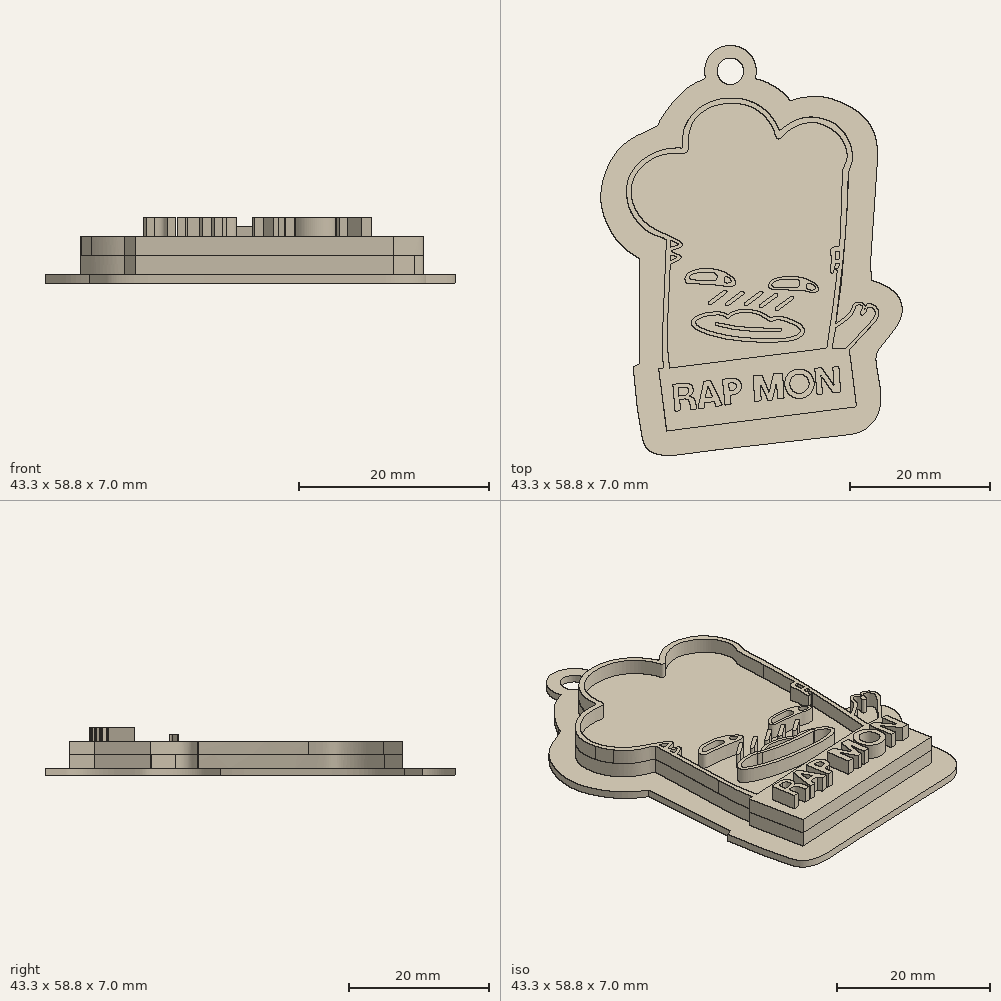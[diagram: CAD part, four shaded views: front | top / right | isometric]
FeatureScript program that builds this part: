
annotation { "Feature Type Name" : "Feature", "Feature Type Description" : "" }
export const myFeature = defineFeature(function(context is Context, id is Id, definition is map)
    precondition{}
    {
        {
            var Q0;
            Q0=qCreatedBy(makeId("Top.planeOp"),FACE);
            var sketch = newSketch(context, id + "F0", { "sketchPlane" : qUnion([Q0])});
            skFitSpline(sketch, "E0", {"points": [v(11.6, -10.29) * mm, v(12.19, -6.25) * mm, v(12.52, -3) * mm, v(12.76, 0) * mm, v(13.08, 4.27) * mm, v(13.3, 8.16) * mm, v(13.44, 11.1) * mm, v(13.87, 12.48) * mm, v(13.83, 14.28) * mm, v(13.03, 16.3) * mm, v(11.52, 17.89) * mm, v(9.06, 18.87) * mm, v(6.77, 18.83) * mm, v(4.71, 17.89) * mm, v(3.64, 17.07) * mm], "startDerivative": vector(7.03, 48) * mm, "endDerivative": vector(-18.68, -15.7) * mm});
            skFitSpline(sketch, "E1", {"points": [v(3.64, 17.07) * mm, v(3.54, 16.95) * mm], "startDerivative": vector(-0.1, -0.12) * mm, "endDerivative": vector(-0.1, -0.12) * mm});
            skFitSpline(sketch, "E2", {"points": [v(3.54, 16.95) * mm, v(3.13, 17.78) * mm, v(2.16, 19.22) * mm, v(0.67, 20.53) * mm, v(-0.94, 21.32) * mm, v(-2.8, 21.68) * mm, v(-4.71, 21.6) * mm, v(-6.36, 21.15) * mm, v(-7.6, 20.54) * mm, v(-8.9, 19.4) * mm, v(-9.89, 18.02) * mm, v(-10.33, 16.75) * mm, v(-10.44, 15.26) * mm, v(-10.47, 14.71) * mm], "startDerivative": vector(-5.85, 12.75) * mm, "endDerivative": vector(-0.6, -9.84) * mm});
            skFitSpline(sketch, "E3", {"points": [v(-10.47, 14.71) * mm, v(-10.48, 14.52) * mm], "startDerivative": vector(-0.01, -0.2) * mm, "endDerivative": vector(-0.01, -0.2) * mm});
            skFitSpline(sketch, "E4", {"points": [v(-10.48, 14.52) * mm, v(-11.68, 14.52) * mm, v(-13.25, 14.28) * mm, v(-14.57, 13.77) * mm, v(-15.75, 13.07) * mm, v(-16.9, 12.1) * mm, v(-17.9, 10.7) * mm, v(-18.43, 9.11) * mm, v(-18.41, 7.32) * mm, v(-18.05, 5.82) * mm, v(-17.34, 4.5) * mm, v(-16.2, 3.19) * mm, v(-14.73, 2.19) * mm, v(-13.46, 1.71) * mm, v(-12.75, 1.35) * mm], "startDerivative": vector(-17.9, 0.57) * mm, "endDerivative": vector(12.96, -6.95) * mm});
            skFitSpline(sketch, "E5", {"points": [v(-12.75, 1.35) * mm, v(-12.75, -0.15) * mm, v(-12.85, -2.56) * mm, v(-13.05, -5.98) * mm, v(-13.18, -9.16) * mm, v(-13.35, -13.7) * mm, v(-13.2, -17.06) * mm], "startDerivative": vector(0.18, -12.05) * mm, "endDerivative": vector(1.35, -17.94) * mm});
            skFitSpline(sketch, "E6", {"points": [v(11.6, -10.29) * mm, v(11.54, -10.75) * mm], "startDerivative": vector(-0.07, -0.47) * mm, "endDerivative": vector(-0.07, -0.47) * mm});
            skFitSpline(sketch, "E7", {"points": [v(11.54, -10.75) * mm, v(12.07, -10.4) * mm, v(12.74, -9.9) * mm, v(13.3, -9.42) * mm, v(13.62, -9.01) * mm, v(13.88, -8.46) * mm, v(14.13, -7.93) * mm, v(14.54, -7.65) * mm, v(15.04, -7.6) * mm, v(15.42, -7.74) * mm, v(15.68, -8) * mm, v(15.76, -8.28) * mm, v(15.68, -8.65) * mm, v(15.45, -9.05) * mm], "startDerivative": vector(6.21, 4.08) * mm, "endDerivative": vector(-2.77, -5.72) * mm});
            skFitSpline(sketch, "E8", {"points": [v(15.45, -9.05) * mm, v(15.72, -8.65) * mm, v(15.86, -8.22) * mm, v(16.04, -7.94) * mm, v(16.33, -7.82) * mm, v(16.83, -7.91) * mm, v(17.31, -8.27) * mm, v(17.64, -8.8) * mm, v(17.72, -9.2) * mm, v(17.63, -9.78) * mm, v(17.29, -10.38) * mm, v(16.76, -10.98) * mm], "startDerivative": vector(3.5, 4.32) * mm, "endDerivative": vector(-4.78, -5.57) * mm});
            skFitSpline(sketch, "E9", {"points": [v(16.76, -10.98) * mm, v(16.27, -11.5) * mm, v(15.56, -12.24) * mm, v(14.69, -13.16) * mm, v(14.2, -13.7) * mm, v(13.62, -14.35) * mm], "startDerivative": vector(-2.64, -2.86) * mm, "endDerivative": vector(-3.05, -3.54) * mm});
            skFitSpline(sketch, "E10", {"points": [v(13.62, -14.35) * mm, v(13.5, -14.48) * mm], "startDerivative": vector(-0.12, -0.13) * mm, "endDerivative": vector(-0.12, -0.13) * mm});
            skLineSegment(sketch, "E11", {"start": v(13.5, -14.48) * mm, "end": v(14.54, -22.61) * mm});
            skLineSegment(sketch, "E12", {"start": v(14.54, -22.61) * mm, "end": v(-12.73, -26.1) * mm});
            skLineSegment(sketch, "E13", {"start": v(-12.73, -26.1) * mm, "end": v(-13.86, -17.17) * mm});
            skLineSegment(sketch, "E14", {"start": v(-13.86, -17.17) * mm, "end": v(-13.32, -17.1) * mm});
            skLineSegment(sketch, "E15", {"start": v(-13.32, -17.1) * mm, "end": v(-13.2, -17.09) * mm});
            skFitSpline(sketch, "E16", {"points": [v(-13.2, -17.06) * mm, v(-13.2, -17.09) * mm], "startDerivative": vector(0, -0.02) * mm, "endDerivative": vector(0, -0.02) * mm});
            skSolve(sketch);
        }
        {
            var Q0;
            Q0 = qSketchRegion(id + "F0", true);
            extrude(context, id + "F1", {"entities" : qUnion([Q0]), "depth" : 2 * mm, "offsetDistance" : 25 * mm});
        }
        {
            var Q0;
            Q0=makeQuery(id+"F1.opExtrude","CAP_FACE",FACE,{"disambiguationData":[OSD([sQuery(id+"F0.wireOp",EDGE,"E0"),sQuery(id+"F0.wireOp",EDGE,"E1"),sQuery(id+"F0.wireOp",EDGE,"E2"),sQuery(id+"F0.wireOp",EDGE,"E3"),sQuery(id+"F0.wireOp",EDGE,"E4"),sQuery(id+"F0.wireOp",EDGE,"E5"),sQuery(id+"F0.wireOp",EDGE,"E6"),sQuery(id+"F0.wireOp",EDGE,"E7"),sQuery(id+"F0.wireOp",EDGE,"E8"),sQuery(id+"F0.wireOp",EDGE,"E9"),sQuery(id+"F0.wireOp",EDGE,"E10"),sQuery(id+"F0.wireOp",EDGE,"E11"),sQuery(id+"F0.wireOp",EDGE,"E12"),sQuery(id+"F0.wireOp",EDGE,"E13"),sQuery(id+"F0.wireOp",EDGE,"E14"),sQuery(id+"F0.wireOp",EDGE,"E15"),sQuery(id+"F0.wireOp",EDGE,"E16")])],"isStart":false});
            var sketch = newSketch(context, id + "F2", { "sketchPlane" : qUnion([Q0])});
            skFitSpline(sketch, "E17", {"points": [v(13.1, -14.2) * mm, v(15, -12.1) * mm, v(16.46, -10.6) * mm, v(17.07, -9.73) * mm, v(17.22, -9.22) * mm, v(16.97, -8.62) * mm, v(16.54, -8.34) * mm, v(16.3, -8.3) * mm, v(16.12, -8.4) * mm, v(16.02, -8.72) * mm, v(15.85, -9.08) * mm, v(15.57, -9.44) * mm], "startDerivative": vector(10.52, 11.7) * mm, "endDerivative": vector(-4.78, -3.46) * mm});
            skFitSpline(sketch, "E18", {"points": [v(15.57, -9.44) * mm, v(15.34, -9.52) * mm, v(15.1, -9.3) * mm, v(15.16, -8.95) * mm], "startDerivative": vector(-0.37, -0.42) * mm, "endDerivative": vector(0.41, 0.7) * mm});
            skFitSpline(sketch, "E19", {"points": [v(15.16, -8.95) * mm, v(15.31, -8.67) * mm, v(15.4, -8.37) * mm, v(15.32, -8.13) * mm, v(15.05, -7.99) * mm, v(14.68, -8.04) * mm, v(14.43, -8.32) * mm, v(14.25, -8.74) * mm, v(14.05, -9.24) * mm, v(13.6, -9.8) * mm, v(12.92, -10.36) * mm, v(12.28, -10.82) * mm, v(11.54, -11.33) * mm], "startDerivative": vector(1.71, 3.54) * mm, "endDerivative": vector(-2.97, -2.1) * mm});
            skFitSpline(sketch, "E20", {"points": [v(11.54, -11.33) * mm, v(11.38, -12.15) * mm, v(11.24, -13.02) * mm, v(11.03, -14.2) * mm], "startDerivative": vector(-0.43, -2.44) * mm, "endDerivative": vector(-0.31, -2.65) * mm});
            skFitSpline(sketch, "E21", {"points": [v(10.26, -14.2) * mm, v(10.89, -10.43) * mm, v(11.16, -8.07) * mm, v(11.5, -5.51) * mm, v(11.76, -3.23) * mm], "startDerivative": vector(2.4, 13.6) * mm, "endDerivative": vector(1.05, 9.74) * mm});
            skFitSpline(sketch, "E22", {"points": [v(11.76, -3.23) * mm, v(11.78, -3.12) * mm], "startDerivative": vector(0.02, 0.11) * mm, "endDerivative": vector(0.02, 0.11) * mm});
            skFitSpline(sketch, "E23", {"points": [v(11.78, -3.12) * mm, v(11.76, -3) * mm, v(11.59, -2.95) * mm, v(11.36, -3) * mm, v(11.27, -3.17) * mm, v(11.23, -3.4) * mm, v(11.1, -3.52) * mm, v(10.9, -3.49) * mm], "startDerivative": vector(0.4, 2.15) * mm, "endDerivative": vector(-1.18, 0.85) * mm});
            skFitSpline(sketch, "E24", {"points": [v(10.9, -3.49) * mm, v(10.79, -3.18) * mm, v(10.8, -2.6) * mm, v(10.9, -1.89) * mm, v(10.9, -1.08) * mm, v(10.8, -0.3) * mm, v(11.03, 0.13) * mm, v(11.43, 0.34) * mm, v(11.8, 0.37) * mm, v(12.01, 0.35) * mm], "startDerivative": vector(-1.67, 3.07) * mm, "endDerivative": vector(2.79, -0.26) * mm});
            skFitSpline(sketch, "E25", {"points": [v(12.01, 0.35) * mm, v(12.1, 0.34) * mm], "startDerivative": vector(0.1, -0.01) * mm, "endDerivative": vector(0.1, -0.01) * mm});
            skFitSpline(sketch, "E26", {"points": [v(12.1, 0.34) * mm, v(12.2, 1.9) * mm, v(12.27, 3.6) * mm, v(12.37, 6.34) * mm], "startDerivative": vector(0.4, 5.25) * mm, "endDerivative": vector(0.28, 7.37) * mm});
            skFitSpline(sketch, "E27", {"points": [v(12.37, 6.34) * mm, v(12.46, 8.71) * mm, v(12.5, 11.04) * mm, v(12.66, 11.63) * mm, v(13.02, 12.46) * mm, v(13.17, 13.54) * mm, v(12.65, 15.38) * mm, v(11.6, 16.7) * mm, v(10.33, 17.59) * mm, v(8.55, 18.17) * mm, v(6.73, 17.95) * mm, v(5.13, 17.22) * mm, v(4.03, 16.28) * mm], "startDerivative": vector(1.15, 22.09) * mm, "endDerivative": vector(-12.74, -12.33) * mm});
            skFitSpline(sketch, "E28", {"points": [v(4.03, 16.28) * mm, v(3.7, 15.92) * mm, v(3.27, 15.82) * mm, v(2.9, 16.28) * mm, v(2.7, 17) * mm, v(2, 18.28) * mm, v(0.5, 19.8) * mm, v(-1.17, 20.63) * mm, v(-2.7, 20.9) * mm, v(-4.51, 20.85) * mm, v(-6.2, 20.43) * mm, v(-7.38, 19.77) * mm, v(-8.41, 18.86) * mm, v(-9.25, 17.5) * mm, v(-9.64, 15.5) * mm, v(-9.62, 14.78) * mm], "startDerivative": vector(-6.82, -9.62) * mm, "endDerivative": vector(1.14, -11.89) * mm});
            skFitSpline(sketch, "E29", {"points": [v(-9.62, 14.78) * mm, v(-9.62, 14.38) * mm, v(-9.78, 13.9) * mm, v(-10.47, 13.8) * mm, v(-11.8, 13.78) * mm, v(-13.46, 13.48) * mm, v(-15.3, 12.58) * mm, v(-16.9, 11.03) * mm, v(-17.72, 9.17) * mm, v(-17.75, 7.3) * mm, v(-17.08, 5.52) * mm, v(-15.62, 3.71) * mm, v(-12.76, 2.1) * mm], "startDerivative": vector(0.36, -9.2) * mm, "endDerivative": vector(25.14, -9.78) * mm});
            skFitSpline(sketch, "E30", {"points": [v(12.1, -0.26) * mm, v(12.05, -1.5) * mm], "startDerivative": vector(-0.05, -1.24) * mm, "endDerivative": vector(-0.05, -1.24) * mm});
            skFitSpline(sketch, "E31", {"points": [v(12.05, -1.5) * mm, v(11.47, -1.5) * mm], "startDerivative": vector(-0.58, 0) * mm, "endDerivative": vector(-0.58, 0) * mm});
            skFitSpline(sketch, "E32", {"points": [v(11.47, -1.5) * mm, v(11.47, -1) * mm, v(11.47, -0.57) * mm, v(11.54, -0.4) * mm, v(11.77, -0.28) * mm, v(12.1, -0.26) * mm], "startDerivative": vector(0.03, 2) * mm, "endDerivative": vector(1.7, -0.01) * mm});
            skFitSpline(sketch, "E33", {"points": [v(11.5, -2.08) * mm, v(12.05, -2.08) * mm], "startDerivative": vector(0.55, 0) * mm, "endDerivative": vector(0.55, 0) * mm});
            skFitSpline(sketch, "E34", {"points": [v(12.05, -2.08) * mm, v(12, -2.7) * mm], "startDerivative": vector(-0.06, -0.62) * mm, "endDerivative": vector(-0.06, -0.62) * mm});
            skFitSpline(sketch, "E35", {"points": [v(12, -2.7) * mm, v(11.4, -2.7) * mm], "startDerivative": vector(-0.59, 0) * mm, "endDerivative": vector(-0.59, 0) * mm});
            skFitSpline(sketch, "E36", {"points": [v(11.5, -2.08) * mm, v(11.4, -2.7) * mm], "startDerivative": vector(-0.1, -0.62) * mm, "endDerivative": vector(-0.1, -0.62) * mm});
            skFitSpline(sketch, "E37", {"points": [v(-12.76, 2.1) * mm, v(-11.31, 1.4) * mm, v(-10.55, 0.91) * mm], "startDerivative": vector(2.75, -1.25) * mm, "endDerivative": vector(1.61, -1.13) * mm});
            skFitSpline(sketch, "E38", {"points": [v(-10.55, 0.91) * mm, v(-10.4, 0.68) * mm, v(-10.55, 0.3) * mm, v(-12.02, -0.28) * mm, v(-11.02, -0.79) * mm, v(-10.7, -1.02) * mm, v(-10.66, -1.28) * mm, v(-12.2, -2.2) * mm], "startDerivative": vector(3.58, -2.62) * mm, "endDerivative": vector(-9.5, -4.38) * mm});
            skLineSegment(sketch, "E39", {"start": v(-12.16, 1.28) * mm, "end": v(-12.16, 0.29) * mm});
            skLineSegment(sketch, "E40", {"start": v(-12.24, -0.82) * mm, "end": v(-12.24, -1.67) * mm});
            skFitSpline(sketch, "E41", {"points": [v(-12.16, 1.28) * mm, v(-11.37, 0.93) * mm, v(-11.03, 0.65) * mm, v(-11.4, 0.48) * mm, v(-12.16, 0.29) * mm], "startDerivative": vector(2.98, -1.12) * mm, "endDerivative": vector(-2.98, -0.56) * mm});
            skFitSpline(sketch, "E42", {"points": [v(-12.24, -0.82) * mm, v(-11.78, -0.9) * mm, v(-11.5, -1) * mm, v(-11.3, -1.17) * mm, v(-11.5, -1.36) * mm, v(-12.24, -1.67) * mm], "startDerivative": vector(2.32, -0.21) * mm, "endDerivative": vector(-2.91, -0.89) * mm});
            skFitSpline(sketch, "E43", {"points": [v(-12.2, -2.2) * mm, v(-12.4, -5.97) * mm, v(-12.56, -9.9) * mm], "startDerivative": vector(-0.41, -7.59) * mm, "endDerivative": vector(-0.3, -7.8) * mm});
            skFitSpline(sketch, "E44", {"points": [v(-12.56, -9.9) * mm, v(-12.63, -13.34) * mm, v(-12.3, -17.06) * mm], "startDerivative": vector(-0.34, -6.97) * mm, "endDerivative": vector(0.86, -7.37) * mm});
            skLineSegment(sketch, "E45", {"start": v(-12.3, -17.06) * mm, "end": v(10.26, -14.2) * mm});
            skLineSegment(sketch, "E46", {"start": v(11.03, -14.2) * mm, "end": v(13.1, -14.2) * mm});
            skFitSpline(sketch, "E47", {"points": [v(-10.48, 14.52) * mm, v(-10.38, 16.33) * mm, v(-10.24, 17.16) * mm, v(-8.91, 19.4) * mm, v(-6.64, 21.04) * mm, v(-4.71, 21.6) * mm, v(-2.8, 21.68) * mm, v(-0.96, 21.32) * mm, v(0.78, 20.45) * mm, v(2, 19.41) * mm, v(2.87, 18.21) * mm, v(3.53, 16.96) * mm], "startDerivative": vector(1.23, 22.38) * mm, "endDerivative": vector(7.77, -15.68) * mm});
            skFitSpline(sketch, "E48", {"points": [v(3.53, 16.96) * mm, v(3.63, 17.08) * mm, v(4.92, 18.03) * mm, v(6.23, 18.66) * mm, v(8.2, 18.97) * mm, v(9.9, 18.66) * mm, v(11.54, 17.91) * mm, v(13.02, 16.3) * mm, v(13.83, 14.28) * mm, v(13.88, 12.47) * mm, v(13.43, 11.07) * mm, v(13.3, 8.15) * mm], "startDerivative": vector(2, 3.3) * mm, "endDerivative": vector(0.47, -26.8) * mm});
            skFitSpline(sketch, "E49", {"points": [v(13.3, 8.15) * mm, v(13.2, 6.11) * mm, v(12.81, 0.56) * mm, v(12.4, -3.18) * mm, v(12.01, -6.7) * mm, v(11.61, -10.29) * mm, v(11.53, -10.75) * mm], "startDerivative": vector(-0.54, -12.33) * mm, "endDerivative": vector(-1.02, -5.08) * mm});
            skFitSpline(sketch, "E50", {"points": [v(11.53, -10.75) * mm, v(12.05, -10.4) * mm, v(12.74, -9.88) * mm, v(13.3, -9.44) * mm, v(13.63, -9) * mm, v(13.88, -8.44) * mm, v(14.13, -7.93) * mm, v(14.56, -7.64) * mm, v(15.1, -7.61) * mm, v(15.49, -7.79) * mm, v(15.73, -8.1) * mm], "startDerivative": vector(4.78, 3.1) * mm, "endDerivative": vector(2.13, -4.2) * mm});
            skFitSpline(sketch, "E51", {"points": [v(15.73, -8.1) * mm, v(15.76, -8.28) * mm, v(15.68, -8.65) * mm, v(15.45, -9.05) * mm], "startDerivative": vector(0.22, -0.62) * mm, "endDerivative": vector(-0.5, -0.98) * mm});
            skFitSpline(sketch, "E52", {"points": [v(15.45, -9.05) * mm, v(15.72, -8.65) * mm, v(15.86, -8.22) * mm, v(15.95, -8.04) * mm, v(16.16, -7.85) * mm, v(16.42, -7.82) * mm, v(16.88, -7.94) * mm, v(17.31, -8.26) * mm, v(17.65, -8.8) * mm, v(17.67, -9.66) * mm, v(17.4, -10.22) * mm, v(16.84, -10.9) * mm, v(16.05, -11.73) * mm, v(15.16, -12.66) * mm, v(13.5, -14.48) * mm], "startDerivative": vector(5.13, 6.12) * mm, "endDerivative": vector(-13.14, -14.52) * mm});
            skLineSegment(sketch, "E53", {"start": v(13.5, -14.48) * mm, "end": v(14.54, -22.61) * mm});
            skLineSegment(sketch, "E54", {"start": v(14.54, -22.61) * mm, "end": v(-12.71, -26.1) * mm});
            skLineSegment(sketch, "E55", {"start": v(-12.71, -26.1) * mm, "end": v(-13.87, -17.17) * mm});
            skLineSegment(sketch, "E56", {"start": v(-13.87, -17.17) * mm, "end": v(-13.2, -17.09) * mm});
            skFitSpline(sketch, "E57", {"points": [v(-13.2, -17.09) * mm, v(-13.36, -13.67) * mm, v(-13.17, -9.16) * mm, v(-13.07, -7.13) * mm, v(-13.01, -5.93) * mm, v(-12.93, -4.2) * mm, v(-12.87, -2.58) * mm, v(-12.82, -1.08) * mm, v(-12.8, -0.1) * mm, v(-12.75, 1.35) * mm], "startDerivative": vector(-1.66, 21.61) * mm, "endDerivative": vector(0.47, 16.04) * mm});
            skFitSpline(sketch, "E58", {"points": [v(-12.75, 1.35) * mm, v(-13.44, 1.7) * mm, v(-14.73, 2.18) * mm, v(-16.19, 3.17) * mm, v(-17.34, 4.5) * mm, v(-18.05, 5.82) * mm, v(-18.42, 7.32) * mm, v(-18.43, 9.12) * mm, v(-17.9, 10.72) * mm, v(-16.9, 12.1) * mm, v(-15.74, 13.1) * mm, v(-14.56, 13.76) * mm, v(-13.23, 14.28) * mm, v(-11.64, 14.52) * mm, v(-10.48, 14.52) * mm], "startDerivative": vector(-12.13, 7.16) * mm, "endDerivative": vector(17.5, -0.46) * mm});
            skSolve(sketch);
        }
        {
            var Q0;
            Q0 = qSketchRegion(id + "F2", true);
            extrude(context, id + "F3", {"entities" : qUnion([Q0]), "operationType" : NewBodyOperationType.ADD, "depth" : 2 * mm, "offsetDistance" : 25 * mm});
        }
        {
            var Q0;
            Q0=makeQuery(id+"F3.boolean.opBoolean","SPLIT",FACE,{"disambiguationData":[TD([makeQuery(id+"F3.opExtrude","SWEPT_FACE",FACE,{"disambiguationData":[OSD([sQuery(id+"F2.wireOp",EDGE,"E21")])]}),makeQuery(id+"F3.opExtrude","SWEPT_FACE",FACE,{"disambiguationData":[OSD([sQuery(id+"F2.wireOp",EDGE,"E22")])]}),makeQuery(id+"F3.opExtrude","SWEPT_FACE",FACE,{"disambiguationData":[OSD([sQuery(id+"F2.wireOp",EDGE,"E23")])]}),makeQuery(id+"F3.opExtrude","SWEPT_FACE",FACE,{"disambiguationData":[OSD([sQuery(id+"F2.wireOp",EDGE,"E24")])]}),makeQuery(id+"F3.opExtrude","SWEPT_FACE",FACE,{"disambiguationData":[OSD([sQuery(id+"F2.wireOp",EDGE,"E25")])]}),makeQuery(id+"F3.opExtrude","SWEPT_FACE",FACE,{"disambiguationData":[OSD([sQuery(id+"F2.wireOp",EDGE,"E26")])]}),makeQuery(id+"F3.opExtrude","SWEPT_FACE",FACE,{"disambiguationData":[OSD([sQuery(id+"F2.wireOp",EDGE,"E27")])]}),makeQuery(id+"F3.opExtrude","SWEPT_FACE",FACE,{"disambiguationData":[OSD([sQuery(id+"F2.wireOp",EDGE,"E28")])]}),makeQuery(id+"F3.opExtrude","SWEPT_FACE",FACE,{"disambiguationData":[OSD([sQuery(id+"F2.wireOp",EDGE,"E29")])]}),makeQuery(id+"F3.opExtrude","SWEPT_FACE",FACE,{"disambiguationData":[OSD([sQuery(id+"F2.wireOp",EDGE,"E37")])]}),makeQuery(id+"F3.opExtrude","SWEPT_FACE",FACE,{"disambiguationData":[OSD([sQuery(id+"F2.wireOp",EDGE,"E38")])]}),makeQuery(id+"F3.opExtrude","SWEPT_FACE",FACE,{"disambiguationData":[OSD([sQuery(id+"F2.wireOp",EDGE,"E43")])]}),makeQuery(id+"F3.opExtrude","SWEPT_FACE",FACE,{"disambiguationData":[OSD([sQuery(id+"F2.wireOp",EDGE,"E44")])]}),makeQuery(id+"F3.opExtrude","SWEPT_FACE",FACE,{"disambiguationData":[OSD([sQuery(id+"F2.wireOp",EDGE,"E45")])]})])],"derivedFrom":makeQuery(id+"F1.opExtrude","CAP_FACE",FACE,{"disambiguationData":[OSD([sQuery(id+"F0.wireOp",EDGE,"E0"),sQuery(id+"F0.wireOp",EDGE,"E1"),sQuery(id+"F0.wireOp",EDGE,"E2"),sQuery(id+"F0.wireOp",EDGE,"E3"),sQuery(id+"F0.wireOp",EDGE,"E4"),sQuery(id+"F0.wireOp",EDGE,"E5"),sQuery(id+"F0.wireOp",EDGE,"E6"),sQuery(id+"F0.wireOp",EDGE,"E7"),sQuery(id+"F0.wireOp",EDGE,"E8"),sQuery(id+"F0.wireOp",EDGE,"E9"),sQuery(id+"F0.wireOp",EDGE,"E10"),sQuery(id+"F0.wireOp",EDGE,"E11"),sQuery(id+"F0.wireOp",EDGE,"E12"),sQuery(id+"F0.wireOp",EDGE,"E13"),sQuery(id+"F0.wireOp",EDGE,"E14"),sQuery(id+"F0.wireOp",EDGE,"E15"),sQuery(id+"F0.wireOp",EDGE,"E16")])],"isStart":false})});
            var sketch = newSketch(context, id + "F4", { "sketchPlane" : qUnion([Q0])});
            skFitSpline(sketch, "E59", {"points": [v(2.14, -4.76) * mm, v(2.8, -4.27) * mm, v(3.8, -4) * mm, v(5.14, -3.92) * mm, v(6.6, -4.04) * mm, v(7.79, -4.48) * mm, v(8.8, -5.15) * mm, v(9.1, -5.83) * mm, v(8.83, -6.12) * mm, v(7.76, -6.14) * mm, v(7.2, -6) * mm, v(4.96, -5.83) * mm, v(2.46, -5.74) * mm, v(1.94, -5.46) * mm, v(2.14, -4.76) * mm]});
            skFitSpline(sketch, "E60", {"points": [v(8.18, -5.03) * mm, v(7.75, -4.85) * mm, v(7.45, -5.05) * mm, v(7.38, -5.57) * mm, v(7.8, -5.82) * mm, v(8.3, -5.87) * mm, v(8.64, -5.71) * mm, v(8.57, -5.38) * mm, v(8.18, -5.03) * mm]});
            skFitSpline(sketch, "E61", {"points": [v(6.01, -4.36) * mm, v(5.12, -4.27) * mm, v(3.87, -4.34) * mm, v(2.92, -4.59) * mm, v(2.53, -4.88) * mm, v(2.38, -5.19) * mm, v(2.54, -5.4) * mm, v(3.17, -5.44) * mm, v(4.02, -5.44) * mm, v(5.07, -5.46) * mm, v(5.77, -5.49) * mm, v(6.2, -5.4) * mm, v(6.38, -5.06) * mm, v(6.37, -4.64) * mm, v(6.01, -4.36) * mm]});
            skFitSpline(sketch, "E62", {"points": [v(-9.8, -3.66) * mm, v(-8.95, -3.1) * mm, v(-7.8, -2.82) * mm, v(-6.05, -2.83) * mm, v(-4.64, -3.2) * mm, v(-3.51, -3.83) * mm, v(-2.85, -4.53) * mm, v(-2.84, -5.08) * mm, v(-3.69, -5.35) * mm, v(-5.5, -5.14) * mm, v(-7.3, -5.02) * mm, v(-8.9, -4.97) * mm, v(-9.71, -4.92) * mm, v(-10.09, -4.4) * mm, v(-9.8, -3.66) * mm]});
            skFitSpline(sketch, "E63", {"points": [v(-4.16, -3.93) * mm, v(-3.7, -4.15) * mm, v(-3.46, -4.68) * mm, v(-4.3, -4.8) * mm, v(-4.46, -4.39) * mm, v(-4.37, -4.01) * mm, v(-4.16, -3.93) * mm]});
            skFitSpline(sketch, "E64", {"points": [v(-5.73, -3.49) * mm, v(-5.5, -3.84) * mm, v(-5.52, -4.3) * mm, v(-5.78, -4.5) * mm, v(-6.86, -4.48) * mm, v(-8.4, -4.41) * mm, v(-9.3, -4.27) * mm, v(-9.36, -3.93) * mm, v(-8.74, -3.52) * mm, v(-7.94, -3.33) * mm, v(-7.08, -3.29) * mm, v(-6.27, -3.32) * mm, v(-5.73, -3.49) * mm]});
            skFitSpline(sketch, "E65", {"points": [v(-3.93, -9.39) * mm, v(-3.24, -9) * mm, v(-2.19, -8.68) * mm, v(-0.83, -8.68) * mm, v(0.48, -8.91) * mm, v(1.54, -9.42) * mm, v(2.31, -9.87) * mm], "startDerivative": vector(4.93, 2.55) * mm, "endDerivative": vector(4.82, -2.88) * mm});
            skFitSpline(sketch, "E66", {"points": [v(2.31, -9.87) * mm, v(2.97, -9.64) * mm, v(4.02, -9.7) * mm, v(5.4, -10.18) * mm, v(6.48, -10.77) * mm, v(7.08, -11.8) * mm, v(6.39, -12.7) * mm, v(5.08, -13.14) * mm, v(3.03, -13.33) * mm, v(0, -13.31) * mm, v(-3.28, -13.04) * mm, v(-5.7, -12.54) * mm, v(-8.63, -11.4) * mm, v(-9.17, -10.58) * mm, v(-8.75, -9.87) * mm, v(-7.72, -9.32) * mm, v(-6.6, -9.07) * mm, v(-5.44, -8.99) * mm, v(-4.52, -9.09) * mm, v(-3.93, -9.39) * mm], "startDerivative": vector(17.15, 7.48) * mm, "endDerivative": vector(15.2, -9.94) * mm});
            skFitSpline(sketch, "E67", {"points": [v(-5.23, -11.03) * mm, v(-3.03, -11.52) * mm, v(0.94, -11.84) * mm, v(3.43, -11.81) * mm], "startDerivative": vector(8.45, -2.15) * mm, "endDerivative": vector(8.47, 0.45) * mm});
            skFitSpline(sketch, "E68", {"points": [v(3.43, -11.81) * mm, v(3.77, -11.7) * mm, v(3.8, -11.46) * mm, v(3.69, -11.33) * mm, v(3.36, -11.33) * mm], "startDerivative": vector(1.61, 0) * mm, "endDerivative": vector(-2.01, -0.19) * mm});
            skFitSpline(sketch, "E69", {"points": [v(3.36, -11.33) * mm, v(1.42, -11.33) * mm, v(-0.8, -11.25) * mm, v(-3.26, -10.97) * mm, v(-5.11, -10.6) * mm], "startDerivative": vector(-6.18, 0.02) * mm, "endDerivative": vector(-8.43, 1.4) * mm});
            skFitSpline(sketch, "E70", {"points": [v(-5.11, -10.6) * mm, v(-5.5, -10.54) * mm, v(-5.7, -10.6) * mm, v(-5.75, -10.77) * mm, v(-5.6, -10.9) * mm, v(-5.23, -11.03) * mm], "startDerivative": vector(-2.11, 0.4) * mm, "endDerivative": vector(1.47, -0.58) * mm});
            skFitSpline(sketch, "E71", {"points": [v(-3.45, -9.64) * mm, v(-3, -9.36) * mm, v(-2.13, -9.11) * mm, v(-1.04, -9.09) * mm, v(0.14, -9.28) * mm, v(1.07, -9.7) * mm, v(1.79, -10.14) * mm, v(2.2, -10.4) * mm, v(2.7, -10.27) * mm], "startDerivative": vector(4.27, 3.73) * mm, "endDerivative": vector(4.72, 2.71) * mm});
            skFitSpline(sketch, "E72", {"points": [v(2.7, -10.27) * mm, v(3.34, -10.11) * mm, v(4.45, -10.4) * mm, v(5.58, -10.84) * mm, v(6.4, -11.48) * mm, v(6.36, -12.04) * mm, v(4.32, -12.75) * mm, v(1.25, -12.85) * mm, v(-1.67, -12.7) * mm, v(-5.1, -12.14) * mm, v(-7.95, -11.17) * mm], "startDerivative": vector(6.5, 3.96) * mm, "endDerivative": vector(-16.8, 8.4) * mm});
            skFitSpline(sketch, "E73", {"points": [v(-7.95, -11.17) * mm, v(-8.32, -10.93) * mm, v(-8.56, -10.56) * mm, v(-8.2, -10.12) * mm, v(-7.7, -9.82) * mm, v(-6.8, -9.58) * mm, v(-5.9, -9.45) * mm, v(-5.23, -9.43) * mm, v(-4.7, -9.52) * mm, v(-4.32, -9.74) * mm, v(-3.9, -9.9) * mm, v(-3.45, -9.64) * mm], "startDerivative": vector(-4.77, 2.89) * mm, "endDerivative": vector(5.66, 5.22) * mm});
            skFitSpline(sketch, "E74", {"points": [v(1.03, -6.5) * mm, v(-0.76, -7.83) * mm], "startDerivative": vector(-1.8, -1.32) * mm, "endDerivative": vector(-1.8, -1.32) * mm});
            skFitSpline(sketch, "E75", {"points": [v(-1.17, -7.46) * mm, v(-1.48, -7.7) * mm, v(-1.54, -7.9) * mm, v(-1.32, -8.1) * mm, v(-1.06, -8.03) * mm, v(-0.76, -7.83) * mm], "startDerivative": vector(-2.6, -2) * mm, "endDerivative": vector(1.48, 1) * mm});
            skFitSpline(sketch, "E76", {"points": [v(-1.17, -7.46) * mm, v(0.6, -6.16) * mm], "startDerivative": vector(1.77, 1.3) * mm, "endDerivative": vector(1.77, 1.3) * mm});
            skFitSpline(sketch, "E77", {"points": [v(0.6, -6.16) * mm, v(0.7, -6.07) * mm, v(0.86, -6.04) * mm, v(1.04, -6.11) * mm, v(1.13, -6.25) * mm, v(1.1, -6.41) * mm, v(1.03, -6.5) * mm], "startDerivative": vector(0.63, 0.6) * mm, "endDerivative": vector(-0.55, -0.58) * mm});
            skFitSpline(sketch, "E78", {"points": [v(3.14, -6.83) * mm, v(1.35, -8.16) * mm], "startDerivative": vector(-1.8, -1.32) * mm, "endDerivative": vector(-1.8, -1.32) * mm});
            skFitSpline(sketch, "E79", {"points": [v(0.94, -7.8) * mm, v(0.63, -8.02) * mm, v(0.57, -8.24) * mm, v(0.8, -8.42) * mm, v(1.05, -8.36) * mm, v(1.35, -8.16) * mm], "startDerivative": vector(-2.6, -2) * mm, "endDerivative": vector(1.48, 1) * mm});
            skFitSpline(sketch, "E80", {"points": [v(0.94, -7.8) * mm, v(2.7, -6.48) * mm], "startDerivative": vector(1.77, 1.3) * mm, "endDerivative": vector(1.77, 1.3) * mm});
            skFitSpline(sketch, "E81", {"points": [v(2.7, -6.48) * mm, v(2.81, -6.4) * mm, v(2.97, -6.37) * mm, v(3.15, -6.44) * mm, v(3.24, -6.58) * mm, v(3.22, -6.74) * mm, v(3.14, -6.83) * mm], "startDerivative": vector(0.63, 0.6) * mm, "endDerivative": vector(-0.55, -0.58) * mm});
            skFitSpline(sketch, "E82", {"points": [v(5.44, -7.23) * mm, v(3.65, -8.55) * mm], "startDerivative": vector(-1.8, -1.32) * mm, "endDerivative": vector(-1.8, -1.32) * mm});
            skFitSpline(sketch, "E83", {"points": [v(3.24, -8.18) * mm, v(2.93, -8.41) * mm, v(2.87, -8.63) * mm, v(3.1, -8.81) * mm, v(3.35, -8.75) * mm, v(3.65, -8.55) * mm], "startDerivative": vector(-2.6, -2) * mm, "endDerivative": vector(1.48, 1) * mm});
            skFitSpline(sketch, "E84", {"points": [v(3.24, -8.18) * mm, v(5, -6.88) * mm], "startDerivative": vector(1.77, 1.3) * mm, "endDerivative": vector(1.77, 1.3) * mm});
            skFitSpline(sketch, "E85", {"points": [v(5, -6.88) * mm, v(5.11, -6.8) * mm, v(5.27, -6.76) * mm, v(5.45, -6.83) * mm, v(5.54, -6.97) * mm, v(5.52, -7.13) * mm, v(5.44, -7.23) * mm], "startDerivative": vector(0.63, 0.6) * mm, "endDerivative": vector(-0.55, -0.58) * mm});
            skFitSpline(sketch, "E86", {"points": [v(-1.69, -6.53) * mm, v(-3.48, -7.86) * mm], "startDerivative": vector(-1.8, -1.32) * mm, "endDerivative": vector(-1.8, -1.32) * mm});
            skFitSpline(sketch, "E87", {"points": [v(-3.89, -7.5) * mm, v(-4.2, -7.72) * mm, v(-4.26, -7.93) * mm, v(-4.03, -8.12) * mm, v(-3.77, -8.06) * mm, v(-3.48, -7.86) * mm], "startDerivative": vector(-2.6, -2) * mm, "endDerivative": vector(1.48, 1) * mm});
            skFitSpline(sketch, "E88", {"points": [v(-3.89, -7.5) * mm, v(-2.12, -6.18) * mm], "startDerivative": vector(1.77, 1.3) * mm, "endDerivative": vector(1.77, 1.3) * mm});
            skFitSpline(sketch, "E89", {"points": [v(-2.12, -6.18) * mm, v(-2.01, -6.1) * mm, v(-1.86, -6.07) * mm, v(-1.68, -6.14) * mm, v(-1.59, -6.28) * mm, v(-1.61, -6.44) * mm, v(-1.69, -6.53) * mm], "startDerivative": vector(0.63, 0.6) * mm, "endDerivative": vector(-0.55, -0.58) * mm});
            skFitSpline(sketch, "E90", {"points": [v(-4.16, -6.38) * mm, v(-5.95, -7.7) * mm], "startDerivative": vector(-1.8, -1.32) * mm, "endDerivative": vector(-1.8, -1.32) * mm});
            skFitSpline(sketch, "E91", {"points": [v(-6.36, -7.34) * mm, v(-6.67, -7.57) * mm, v(-6.73, -7.79) * mm, v(-6.5, -7.97) * mm, v(-6.25, -7.91) * mm, v(-5.95, -7.7) * mm], "startDerivative": vector(-2.6, -2) * mm, "endDerivative": vector(1.48, 1) * mm});
            skFitSpline(sketch, "E92", {"points": [v(-6.36, -7.34) * mm, v(-4.6, -6.03) * mm], "startDerivative": vector(1.77, 1.3) * mm, "endDerivative": vector(1.77, 1.3) * mm});
            skFitSpline(sketch, "E93", {"points": [v(-4.6, -6.03) * mm, v(-4.49, -5.95) * mm, v(-4.33, -5.92) * mm, v(-4.16, -5.99) * mm, v(-4.06, -6.13) * mm, v(-4.09, -6.29) * mm, v(-4.16, -6.38) * mm], "startDerivative": vector(0.63, 0.6) * mm, "endDerivative": vector(-0.55, -0.58) * mm});
            skSolve(sketch);
        }
        {
            var Q0;
            Q0 = qSketchRegion(id + "F4", true);
            extrude(context, id + "F5", {"entities" : qUnion([Q0]), "operationType" : NewBodyOperationType.ADD, "depth" : 2 * mm, "offsetDistance" : 25 * mm});
        }
        {
            var Q0;
            Q0=makeQuery(id+"F4.imprint","IMPRINT",FACE,{"disambiguationData":[TD([[makeQuery(id+"F4.imprint","IMPRINT",EDGE,{"derivedFrom":sQuery(id+"F4.wireOp",EDGE,"E67")}),1.0]])]});
            extrude(context, id + "F6", {"entities" : qUnion([Q0]), "operationType" : NewBodyOperationType.ADD, "depth" : 3 * mm, "offsetDistance" : 25 * mm});
        }
        {
            var Q0;
            Q0=makeQuery(id+"F3.opExtrude","CAP_FACE",FACE,{"disambiguationData":[OSD([sQuery(id+"F2.wireOp",EDGE,"E17"),sQuery(id+"F2.wireOp",EDGE,"E18"),sQuery(id+"F2.wireOp",EDGE,"E19"),sQuery(id+"F2.wireOp",EDGE,"E20"),sQuery(id+"F2.wireOp",EDGE,"E21"),sQuery(id+"F2.wireOp",EDGE,"E22"),sQuery(id+"F2.wireOp",EDGE,"E23"),sQuery(id+"F2.wireOp",EDGE,"E24"),sQuery(id+"F2.wireOp",EDGE,"E25"),sQuery(id+"F2.wireOp",EDGE,"E26"),sQuery(id+"F2.wireOp",EDGE,"E27"),sQuery(id+"F2.wireOp",EDGE,"E28"),sQuery(id+"F2.wireOp",EDGE,"E29"),sQuery(id+"F2.wireOp",EDGE,"E30"),sQuery(id+"F2.wireOp",EDGE,"E31"),sQuery(id+"F2.wireOp",EDGE,"E32"),sQuery(id+"F2.wireOp",EDGE,"E33"),sQuery(id+"F2.wireOp",EDGE,"E34"),sQuery(id+"F2.wireOp",EDGE,"E35"),sQuery(id+"F2.wireOp",EDGE,"E36"),sQuery(id+"F2.wireOp",EDGE,"E37"),sQuery(id+"F2.wireOp",EDGE,"E38"),sQuery(id+"F2.wireOp",EDGE,"E39"),sQuery(id+"F2.wireOp",EDGE,"E40"),sQuery(id+"F2.wireOp",EDGE,"E41"),sQuery(id+"F2.wireOp",EDGE,"E42"),sQuery(id+"F2.wireOp",EDGE,"E43"),sQuery(id+"F2.wireOp",EDGE,"E44"),sQuery(id+"F2.wireOp",EDGE,"E45"),sQuery(id+"F2.wireOp",EDGE,"E46"),sQuery(id+"F2.wireOp",EDGE,"E47"),sQuery(id+"F2.wireOp",EDGE,"E48"),sQuery(id+"F2.wireOp",EDGE,"E49"),sQuery(id+"F2.wireOp",EDGE,"E50"),sQuery(id+"F2.wireOp",EDGE,"E51"),sQuery(id+"F2.wireOp",EDGE,"E52"),sQuery(id+"F2.wireOp",EDGE,"E53"),sQuery(id+"F2.wireOp",EDGE,"E54"),sQuery(id+"F2.wireOp",EDGE,"E55"),sQuery(id+"F2.wireOp",EDGE,"E56"),sQuery(id+"F2.wireOp",EDGE,"E57"),sQuery(id+"F2.wireOp",EDGE,"E58")])],"isStart":false});
            var sketch = newSketch(context, id + "F7", { "sketchPlane" : qUnion([Q0])});
            skLineSegment(sketch, "E94", {"start": v(-11.84, -19.39) * mm, "end": v(-11.52, -23.25) * mm});
            skLineSegment(sketch, "E95", {"start": v(-11.52, -23.25) * mm, "end": v(-10.72, -23.18) * mm});
            skLineSegment(sketch, "E96", {"start": v(-10.72, -23.18) * mm, "end": v(-10.85, -21.6) * mm});
            skFitSpline(sketch, "E97", {"points": [v(-10.85, -21.6) * mm, v(-10.48, -21.53) * mm, v(-10.14, -21.49) * mm, v(-9.69, -21.6) * mm, v(-9.36, -22.26) * mm, v(-9.32, -23.03) * mm], "startDerivative": vector(1.51, 0.56) * mm, "endDerivative": vector(0.07, -3.2) * mm});
            skLineSegment(sketch, "E98", {"start": v(-9.32, -23.03) * mm, "end": v(-8.42, -22.95) * mm});
            skLineSegment(sketch, "E99", {"start": v(-11.84, -19.39) * mm, "end": v(-10, -19.23) * mm});
            skLineSegment(sketch, "E100", {"start": v(-11.06, -19.86) * mm, "end": v(-10.96, -21.07) * mm});
            skLineSegment(sketch, "E101", {"start": v(-10.96, -21.07) * mm, "end": v(-10.11, -21) * mm});
            skLineSegment(sketch, "E102", {"start": v(-11.06, -19.86) * mm, "end": v(-10.3, -19.8) * mm});
            skFitSpline(sketch, "E103", {"points": [v(-9.4, -21.16) * mm, v(-9.06, -21.25) * mm, v(-8.66, -21.65) * mm, v(-8.5, -22.36) * mm, v(-8.42, -22.95) * mm], "startDerivative": vector(1.68, -0.2) * mm, "endDerivative": vector(0.3, -2.18) * mm});
            skFitSpline(sketch, "E104", {"points": [v(-10, -19.23) * mm, v(-9.78, -19.23) * mm, v(-9.36, -19.36) * mm, v(-9.01, -19.73) * mm, v(-8.93, -20.54) * mm, v(-9.2, -20.91) * mm, v(-9.5, -21.08) * mm], "startDerivative": vector(2.7, 0) * mm, "endDerivative": vector(-2.39, -0.95) * mm});
            skFitSpline(sketch, "E105", {"points": [v(-9.5, -21.08) * mm, v(-9.56, -21.14) * mm], "startDerivative": vector(-0.16, -0.06) * mm, "endDerivative": vector(0.13, 0) * mm});
            skFitSpline(sketch, "E106", {"points": [v(-9.4, -21.16) * mm, v(-9.56, -21.14) * mm], "startDerivative": vector(-0.16, 0.02) * mm, "endDerivative": vector(-0.16, 0.02) * mm});
            skFitSpline(sketch, "E107", {"points": [v(-10.3, -19.8) * mm, v(-9.96, -19.8) * mm, v(-9.65, -19.97) * mm, v(-9.54, -20.33) * mm, v(-9.58, -20.63) * mm, v(-10.11, -21) * mm], "startDerivative": vector(2.39, -0.04) * mm, "endDerivative": vector(-4.11, -1.05) * mm});
            skLineSegment(sketch, "E108", {"start": v(-7.36, -18.94) * mm, "end": v(-8.24, -22.92) * mm});
            skLineSegment(sketch, "E109", {"start": v(-8.24, -22.92) * mm, "end": v(-7.36, -22.86) * mm});
            skLineSegment(sketch, "E110", {"start": v(-7.36, -18.94) * mm, "end": v(-6.4, -18.84) * mm});
            skLineSegment(sketch, "E111", {"start": v(-6.4, -18.84) * mm, "end": v(-4.7, -22.42) * mm});
            skLineSegment(sketch, "E112", {"start": v(-4.7, -22.42) * mm, "end": v(-5.61, -22.57) * mm});
            skLineSegment(sketch, "E113", {"start": v(-5.61, -22.57) * mm, "end": v(-5.9, -21.9) * mm});
            skLineSegment(sketch, "E114", {"start": v(-5.9, -21.9) * mm, "end": v(-7.24, -21.98) * mm});
            skLineSegment(sketch, "E115", {"start": v(-7.24, -21.98) * mm, "end": v(-7.36, -22.86) * mm});
            skLineSegment(sketch, "E116", {"start": v(-6.81, -19.68) * mm, "end": v(-7.18, -21.32) * mm});
            skLineSegment(sketch, "E117", {"start": v(-7.18, -21.32) * mm, "end": v(-6.07, -21.25) * mm});
            skLineSegment(sketch, "E118", {"start": v(-6.07, -21.25) * mm, "end": v(-6.81, -19.68) * mm});
            skLineSegment(sketch, "E119", {"start": v(-4.72, -18.67) * mm, "end": v(-4.34, -22.37) * mm});
            skLineSegment(sketch, "E120", {"start": v(-4.34, -22.37) * mm, "end": v(-3.48, -22.29) * mm});
            skLineSegment(sketch, "E121", {"start": v(-3.48, -22.29) * mm, "end": v(-3.61, -20.95) * mm});
            skLineSegment(sketch, "E122", {"start": v(-3.61, -20.95) * mm, "end": v(-3.1, -20.9) * mm});
            skLineSegment(sketch, "E123", {"start": v(-4.72, -18.67) * mm, "end": v(-3.3, -18.53) * mm});
            skLineSegment(sketch, "E124", {"start": v(-3.84, -19.25) * mm, "end": v(-3.73, -20.3) * mm});
            skArc(sketch, "E125", {"start": v(-3.1, -20.9) * mm, "mid": v(-1.99, -19.61) * mm, "end": v(-3.3, -18.53) * mm});
            skFitSpline(sketch, "E126", {"points": [v(-3.84, -19.25) * mm, v(-3.3, -19.18) * mm, v(-2.98, -19.25) * mm, v(-2.72, -19.59) * mm, v(-2.83, -20.09) * mm, v(-3.29, -20.25) * mm, v(-3.73, -20.3) * mm], "startDerivative": vector(3.02, 0.88) * mm, "endDerivative": vector(-2.6, -0.15) * mm});
            skLineSegment(sketch, "E127", {"start": v(-0.33, -18.14) * mm, "end": v(-0.08, -21.82) * mm});
            skLineSegment(sketch, "E128", {"start": v(-0.08, -21.82) * mm, "end": v(0.86, -21.76) * mm});
            skLineSegment(sketch, "E129", {"start": v(0.86, -21.76) * mm, "end": v(0.69, -19.3) * mm});
            skLineSegment(sketch, "E130", {"start": v(0.69, -19.3) * mm, "end": v(1.84, -21.69) * mm});
            skLineSegment(sketch, "E131", {"start": v(1.84, -21.69) * mm, "end": v(2.46, -21.63) * mm});
            skLineSegment(sketch, "E132", {"start": v(-0.33, -18.14) * mm, "end": v(0.94, -18.05) * mm});
            skLineSegment(sketch, "E133", {"start": v(0.94, -18.05) * mm, "end": v(2, -20.55) * mm});
            skLineSegment(sketch, "E134", {"start": v(2, -20.55) * mm, "end": v(2.62, -17.85) * mm});
            skLineSegment(sketch, "E135", {"start": v(2.62, -17.85) * mm, "end": v(3.92, -17.78) * mm});
            skLineSegment(sketch, "E136", {"start": v(3.92, -17.78) * mm, "end": v(4.12, -21.42) * mm});
            skLineSegment(sketch, "E137", {"start": v(4.12, -21.42) * mm, "end": v(3.19, -21.47) * mm});
            skLineSegment(sketch, "E138", {"start": v(3.19, -21.47) * mm, "end": v(3.05, -19.1) * mm});
            skLineSegment(sketch, "E139", {"start": v(3.05, -19.1) * mm, "end": v(2.46, -21.63) * mm});
            skCircle(sketch, "E140", {"center": v(6.34, -19.33) * mm, "radius": 1.38 * mm});
            skCircle(sketch, "E141", {"center": v(6.34, -19.33) * mm, "radius": 2.12 * mm});
            skLineSegment(sketch, "E142", {"start": v(8.52, -17.07) * mm, "end": v(8.88, -20.9) * mm});
            skLineSegment(sketch, "E143", {"start": v(8.88, -20.9) * mm, "end": v(9.67, -20.83) * mm});
            skLineSegment(sketch, "E144", {"start": v(9.67, -20.83) * mm, "end": v(9.42, -18.12) * mm});
            skLineSegment(sketch, "E145", {"start": v(9.42, -18.12) * mm, "end": v(11.17, -20.64) * mm});
            skLineSegment(sketch, "E146", {"start": v(11.17, -20.64) * mm, "end": v(12.25, -20.56) * mm});
            skLineSegment(sketch, "E147", {"start": v(12.25, -20.56) * mm, "end": v(12, -16.86) * mm});
            skLineSegment(sketch, "E148", {"start": v(12, -16.86) * mm, "end": v(11.12, -16.92) * mm});
            skLineSegment(sketch, "E149", {"start": v(11.12, -16.92) * mm, "end": v(11.3, -19.61) * mm});
            skLineSegment(sketch, "E150", {"start": v(11.3, -19.61) * mm, "end": v(9.53, -17.02) * mm});
            skLineSegment(sketch, "E151", {"start": v(9.53, -17.02) * mm, "end": v(8.52, -17.07) * mm});
            skSolve(sketch);
        }
        {
            var Q0;
            Q0 = qSketchRegion(id + "F7", true);
            extrude(context, id + "F8", {"entities" : qUnion([Q0]), "operationType" : NewBodyOperationType.ADD, "depth" : 2 * mm, "offsetDistance" : 25 * mm});
        }
        {
            var Q0;
            Q0=makeQuery(id+"F1.opExtrude","CAP_FACE",FACE,{"disambiguationData":[OSD([sQuery(id+"F0.wireOp",EDGE,"E0"),sQuery(id+"F0.wireOp",EDGE,"E1"),sQuery(id+"F0.wireOp",EDGE,"E2"),sQuery(id+"F0.wireOp",EDGE,"E3"),sQuery(id+"F0.wireOp",EDGE,"E4"),sQuery(id+"F0.wireOp",EDGE,"E5"),sQuery(id+"F0.wireOp",EDGE,"E6"),sQuery(id+"F0.wireOp",EDGE,"E7"),sQuery(id+"F0.wireOp",EDGE,"E8"),sQuery(id+"F0.wireOp",EDGE,"E9"),sQuery(id+"F0.wireOp",EDGE,"E10"),sQuery(id+"F0.wireOp",EDGE,"E11"),sQuery(id+"F0.wireOp",EDGE,"E12"),sQuery(id+"F0.wireOp",EDGE,"E13"),sQuery(id+"F0.wireOp",EDGE,"E14"),sQuery(id+"F0.wireOp",EDGE,"E15"),sQuery(id+"F0.wireOp",EDGE,"E16")])],"isStart":true});
            var sketch = newSketch(context, id + "F9", { "sketchPlane" : qUnion([Q0])});
            skFitSpline(sketch, "E152", {"points": [v(-7.13, -24.5) * mm, v(-9.4, -23.34) * mm, v(-11.96, -20.86) * mm, v(-13.7, -18.38) * mm], "startDerivative": vector(-7.39, 3.06) * mm, "endDerivative": vector(-4.75, 7.37) * mm});
            skFitSpline(sketch, "E153", {"points": [v(-13.7, -18.38) * mm, v(-13.95, -17.7) * mm], "startDerivative": vector(-0.25, 0.68) * mm, "endDerivative": vector(-0.25, 0.68) * mm});
            skFitSpline(sketch, "E154", {"points": [v(-13.95, -17.7) * mm, v(-16.56, -16.5) * mm, v(-19.85, -13.97) * mm, v(-22.16, -8.11) * mm, v(-21.23, -3.55) * mm, v(-18.9, -0.27) * mm, v(-16.67, 1.3) * mm], "startDerivative": vector(-18.07, 7.9) * mm, "endDerivative": vector(8.98, 4.18) * mm});
            skFitSpline(sketch, "E155", {"points": [v(-16.67, 1.3) * mm, v(-16.67, 11.58) * mm, v(-16.67, 16.53) * mm], "startDerivative": vector(0, 18.98) * mm, "endDerivative": vector(0, 11) * mm});
            skFitSpline(sketch, "E156", {"points": [v(-16.67, 16.53) * mm, v(-17.53, 16.89) * mm], "startDerivative": vector(-0.86, 0.36) * mm, "endDerivative": vector(-0.86, 0.36) * mm});
            skFitSpline(sketch, "E157", {"points": [v(-17.53, 16.89) * mm, v(-16.46, 25.86) * mm, v(-15.4, 28.75) * mm, v(-12.58, 29.6) * mm, v(-6.87, 28.96) * mm, v(2.8, 27.9) * mm, v(11.96, 26.78) * mm, v(15.13, 26.21) * mm, v(17.39, 24.17) * mm, v(17.95, 20.22) * mm, v(17.32, 16) * mm, v(17.88, 14.23) * mm, v(20.77, 10.2) * mm, v(20.63, 6.97) * mm, v(18.55, 5.18) * mm, v(16.68, 4.5) * mm], "startDerivative": vector(6.33, 109.7) * mm, "endDerivative": vector(-40.7, -10.86) * mm});
            skFitSpline(sketch, "E158", {"points": [v(16.68, 4.5) * mm, v(16.64, 0.26) * mm, v(17.12, -5.67) * mm, v(17.41, -10.84) * mm, v(17.27, -16) * mm, v(15.35, -19.22) * mm, v(12.5, -21) * mm, v(9.36, -21.92) * mm, v(6.19, -21.65) * mm], "startDerivative": vector(-3.51, -33.86) * mm, "endDerivative": vector(-29.25, 4.94) * mm});
            skFitSpline(sketch, "E159", {"points": [v(6.19, -21.65) * mm, v(5, -21.23) * mm], "startDerivative": vector(-1.19, 0.42) * mm, "endDerivative": vector(-1.19, 0.42) * mm});
            skFitSpline(sketch, "E160", {"points": [v(5, -21.23) * mm, v(3, -23.18) * mm, v(0, -24.47) * mm], "startDerivative": vector(-2.58, -5.26) * mm, "endDerivative": vector(-7.29, -1.31) * mm});
            skArc(sketch, "E161", {"start": v(-7.13, -24.5) * mm, "mid": v(-3.55, -29.24) * mm, "end": v(0, -24.47) * mm});
            skCircle(sketch, "E162", {"center": v(-3.56, -25.52) * mm, "radius": 1.9 * mm});
            skSolve(sketch);
        }
        {
            var Q0;
            Q0 = qSketchRegion(id + "F9", true);
            extrude(context, id + "F10", {"entities" : qUnion([Q0]), "operationType" : NewBodyOperationType.ADD, "depth" : 1 * mm, "offsetDistance" : 25 * mm});
        }
    });
